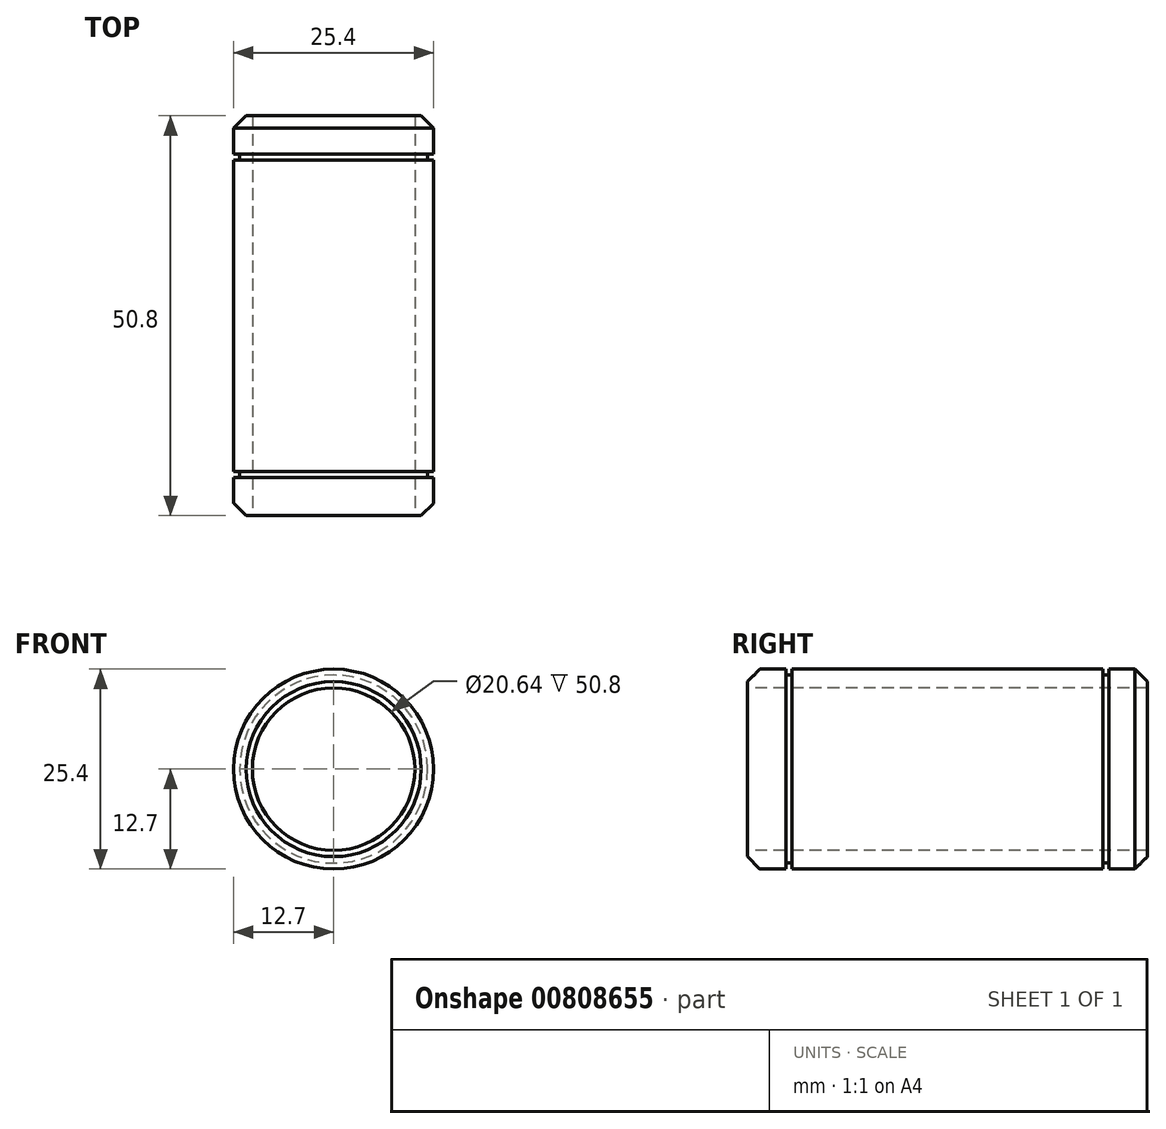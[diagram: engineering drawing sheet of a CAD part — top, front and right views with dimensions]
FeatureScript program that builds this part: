
annotation { "Feature Type Name" : "Feature", "Feature Type Description" : "" }
export const myFeature = defineFeature(function(context is Context, id is Id, definition is map)
    precondition{}
    {
        {
            var Q0;
            Q0=qCreatedBy(makeId("Front.planeOp"),FACE);
            var sketch = newSketch(context, id + "F0", { "sketchPlane" : qUnion([Q0])});
            skCircle(sketch, "E0", {"center": v(0, 0) * mm, "radius": 12.7 * mm});
            skSolve(sketch);
        }
        {
            var Q0;
            Q0=makeQuery(id+"F0.imprint","IMPRINT",FACE,{"disambiguationData":[TD([[makeQuery(id+"F0.imprint","IMPRINT",EDGE,{"derivedFrom":sQuery(id+"F0.wireOp",EDGE,"E0")}),1.0]])]});
            extrude(context, id + "F1", {"entities" : qUnion([Q0]), "depth" : 50.8 * mm, "offsetDistance" : 25.4 * mm});
        }
        {
            var Q0;
            Q0=makeQuery(id+"F1.opExtrude","CAP_EDGE",EDGE,{"disambiguationData":[OSD([sQuery(id+"F0.wireOp",EDGE,"E0")])],"isStart":false});
            var Q1;
            Q1=makeQuery(id+"F1.opExtrude","CAP_EDGE",EDGE,{"disambiguationData":[OSD([sQuery(id+"F0.wireOp",EDGE,"E0")])],"isStart":true});
            chamfer(context, id + "F2", {"entities" : qUnion([Q0, Q1]), "width" : 1.59 * mm, "tangentPropagation" : true});
        }
        {
            var Q0;
            Q0=qCreatedBy(makeId("Right.planeOp"),FACE);
            var sketch = newSketch(context, id + "F3", { "sketchPlane" : qUnion([Q0])});
            skLineSegment(sketch, "E1", {"start": v(-55.34, 11.94) * mm, "end": v(4.18, 11.94) * mm, "construction": true});
            skLineSegment(sketch, "E2", {"start": v(-5.64, 18.93) * mm, "end": v(-5.64, -15.93) * mm, "construction": true});
            skPoint(sketch, "E3", {"position": v(-5.64, 11.94) * mm});
            skLineSegment(sketch, "E4.bottom", {"start": v(-5.64, 11.94) * mm, "end": v(-4.88, 11.94) * mm});
            skLineSegment(sketch, "E4.top", {"start": v(-5.64, 13.75) * mm, "end": v(-4.88, 13.75) * mm});
            skLineSegment(sketch, "E4.left", {"start": v(-5.64, 11.94) * mm, "end": v(-5.64, 13.75) * mm});
            skLineSegment(sketch, "E4.right", {"start": v(-4.88, 11.94) * mm, "end": v(-4.88, 13.75) * mm});
            skLineSegment(sketch, "E5", {"start": v(-25.4, 20.5) * mm, "end": v(-25.4, -16.94) * mm, "construction": true});
            skLineSegment(sketch, "E6.MirrorCS", {"start": v(-45.16, 11.94) * mm, "end": v(-45.16, 13.75) * mm});
            skLineSegment(sketch, "E7.MirrorCS", {"start": v(-45.92, 11.94) * mm, "end": v(-45.92, 13.75) * mm});
            skLineSegment(sketch, "E8.MirrorCS", {"start": v(-45.16, 11.94) * mm, "end": v(-45.92, 11.94) * mm});
            skLineSegment(sketch, "E9.MirrorCS", {"start": v(-45.16, 13.75) * mm, "end": v(-45.92, 13.75) * mm});
            skPoint(sketch, "E10.MirrorP", {"position": v(-45.16, 11.94) * mm});
            skSolve(sketch);
        }
        {
            var Q0;
            Q0=qCreatedBy(makeId("Right.planeOp"),FACE);
            var sketch = newSketch(context, id + "F4", { "sketchPlane" : qUnion([Q0])});
            skLineSegment(sketch, "E11", {"start": v(0, 0) * mm, "end": v(-55.85, 0) * mm, "construction": true});
            skSolve(sketch);
        }
        {
            var Q0;
            Q0=makeQuery(id+"F3.imprint","IMPRINT",FACE,{"disambiguationData":[TD([[makeQuery(id+"F3.imprint","IMPRINT",EDGE,{"derivedFrom":sQuery(id+"F3.wireOp",EDGE,"E6.MirrorCS")}),1.0]])]});
            var Q1;
            Q1=makeQuery(id+"F3.imprint","IMPRINT",FACE,{"disambiguationData":[TD([[makeQuery(id+"F3.imprint","IMPRINT",EDGE,{"derivedFrom":sQuery(id+"F3.wireOp",EDGE,"E4.bottom")}),1.0]])]});
            var Q2;
            Q2=sQuery(id+"F4.wireOp",EDGE,"E11");
            revolve(context, id + "F5", {"operationType" : NewBodyOperationType.REMOVE, "surfaceOperationType" : NewSurfaceOperationType.NEW, "entities" : qUnion([Q0, Q1]), "axis" : qUnion([Q2]), "revolveType" : RevolveType.FULL, "oppositeDirection" : true});
        }
        {
            var Q0;
            {var subQ0=sQuery(id+"F0.wireOp",EDGE,"E0");Q0=makeQuery(id+"F2.opChamfer","BLEND_EDGE",EDGE,{"blendedFrom":[makeQuery(id+"F1.opExtrude","CAP_EDGE",EDGE,{"disambiguationData":[OSD([subQ0])],"isStart":false}),makeQuery(id+"F1.opExtrude","SWEPT_FACE",FACE,{"disambiguationData":[OSD([subQ0])]})],"blendedInto":[makeQuery(id+"F1.opExtrude","SWEPT_FACE",FACE,{"disambiguationData":[OSD([subQ0])]})]});}
            fillet(context, id + "F6", {"entities" : qUnion([Q0]), "radius" : 0.13 * mm, "tangentPropagation" : true, "allowEdgeOverflow" : false});
        }
        {
            var Q0;
            Q0=makeQuery(id+"F1.opExtrude","CAP_FACE",FACE,{"disambiguationData":[OSD([sQuery(id+"F0.wireOp",EDGE,"E0")])],"isStart":false});
            var sketch = newSketch(context, id + "F7", { "sketchPlane" : qUnion([Q0])});
            skCircle(sketch, "E12", {"center": v(0, 0) * mm, "radius": 10.32 * mm});
            skSolve(sketch);
        }
        {
            var Q0;
            Q0=makeQuery(id+"F7.imprint","IMPRINT",FACE,{"disambiguationData":[TD([[makeQuery(id+"F7.imprint","IMPRINT",EDGE,{"derivedFrom":sQuery(id+"F7.wireOp",EDGE,"E12")}),1.0]])]});
            extrude(context, id + "F8", {"entities" : qUnion([Q0]), "operationType" : NewBodyOperationType.REMOVE, "endBound" : BoundingType.THROUGH_ALL, "oppositeDirection" : true, "depth" : 25.4 * mm, "offsetDistance" : 25.4 * mm});
        }
    });
